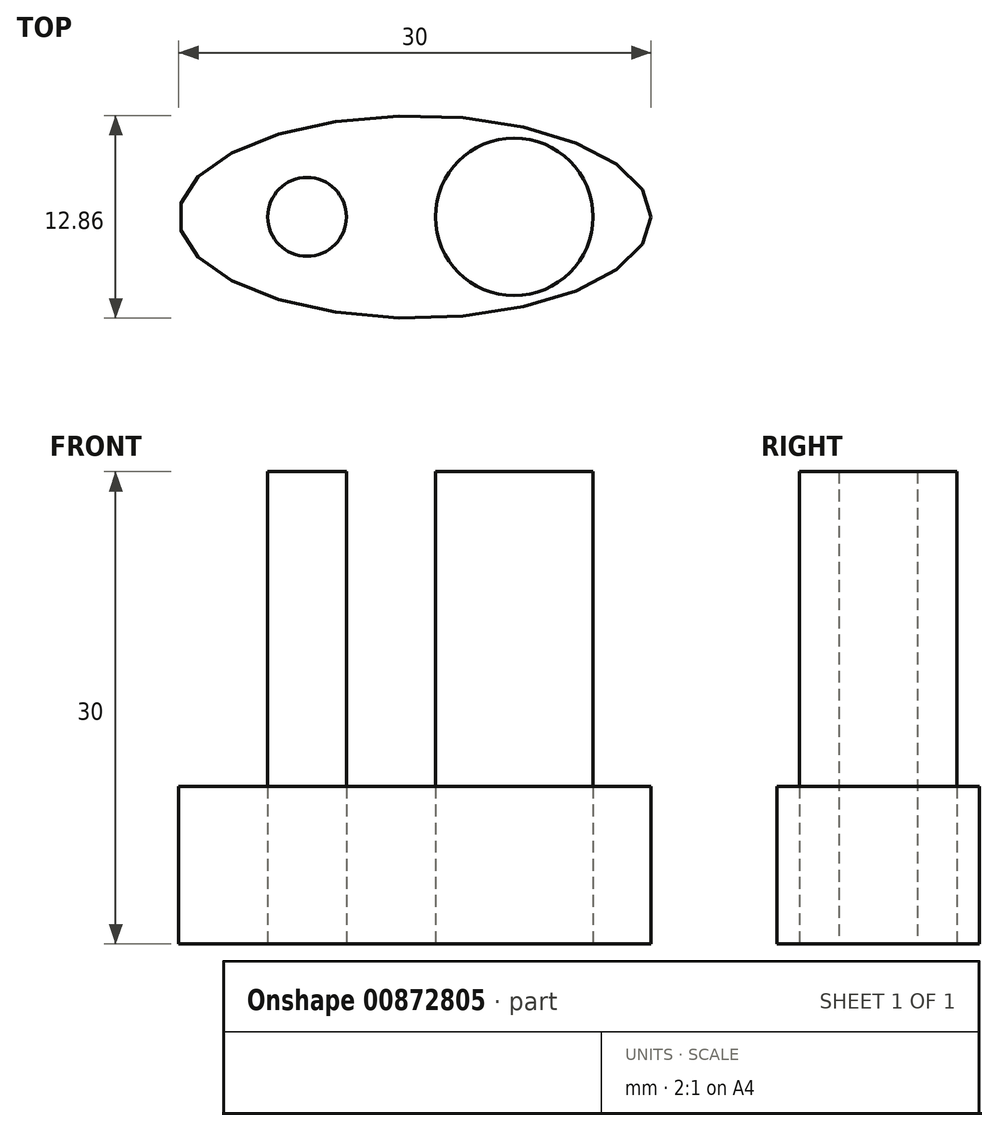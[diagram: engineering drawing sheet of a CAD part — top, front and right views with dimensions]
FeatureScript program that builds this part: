
annotation { "Feature Type Name" : "Feature", "Feature Type Description" : "" }
export const myFeature = defineFeature(function(context is Context, id is Id, definition is map)
    precondition{}
    {
        {
            var Q0;
            Q0=qCreatedBy(makeId("Top.planeOp"),FACE);
            var sketch = newSketch(context, id + "F0", { "sketchPlane" : qUnion([Q0])});
            skEllipse(sketch, "E0", {"center": v(0, 0) * mm, "majorRadius": 15 * mm, "minorRadius": 6.43 * mm, "majorAxis": v(1, 0)});
            skSolve(sketch);
        }
        {
            var Q0;
            Q0=makeQuery(id+"F0.imprint","IMPRINT",FACE,{"disambiguationData":[TD([[makeQuery(id+"F0.imprint","IMPRINT",EDGE,{"derivedFrom":sQuery(id+"F0.wireOp",EDGE,"E0")}),1.0]])]});
            var sketch = newSketch(context, id + "F1", { "sketchPlane" : qUnion([Q0])});
            skCircle(sketch, "E1", {"center": v(-6.85, 0) * mm, "radius": 2.5 * mm});
            skCircle(sketch, "E2", {"center": v(6.3, 0) * mm, "radius": 5 * mm});
            skSolve(sketch);
        }
        {
            var Q0;
            Q0=makeQuery(id+"F1.imprint","IMPRINT",FACE,{"disambiguationData":[TD([[makeQuery(id+"F1.imprint","IMPRINT",EDGE,{"derivedFrom":sQuery(id+"F1.wireOp",EDGE,"E2")}),1.0]])]});
            var Q1;
            Q1=makeQuery(id+"F1.imprint","IMPRINT",FACE,{"disambiguationData":[TD([[makeQuery(id+"F1.imprint","IMPRINT",EDGE,{"derivedFrom":sQuery(id+"F1.wireOp",EDGE,"E1")}),1.0]])]});
            var Q2;
            Q2=sQuery(id+"F1.wireOp",EDGE,"E2");
            var Q3;
            Q3=sQuery(id+"F1.wireOp",EDGE,"E1");
            extrude(context, id + "F2", {"entities" : qUnion([Q0, Q1]), "surfaceEntities" : qUnion([Q2, Q3]), "depth" : 30 * mm, "offsetDistance" : 25 * mm});
        }
        {
            var Q0;
            Q0=makeQuery(id+"F0.imprint","IMPRINT",FACE,{"disambiguationData":[TD([[makeQuery(id+"F0.imprint","IMPRINT",EDGE,{"derivedFrom":sQuery(id+"F0.wireOp",EDGE,"E0")}),1.0]])]});
            var Q1;
            Q1=sQuery(id+"F0.wireOp",EDGE,"E0");
            extrude(context, id + "F3", {"entities" : qUnion([Q0]), "surfaceEntities" : qUnion([Q1]), "depth" : 10 * mm, "offsetDistance" : 25 * mm});
        }
    });
